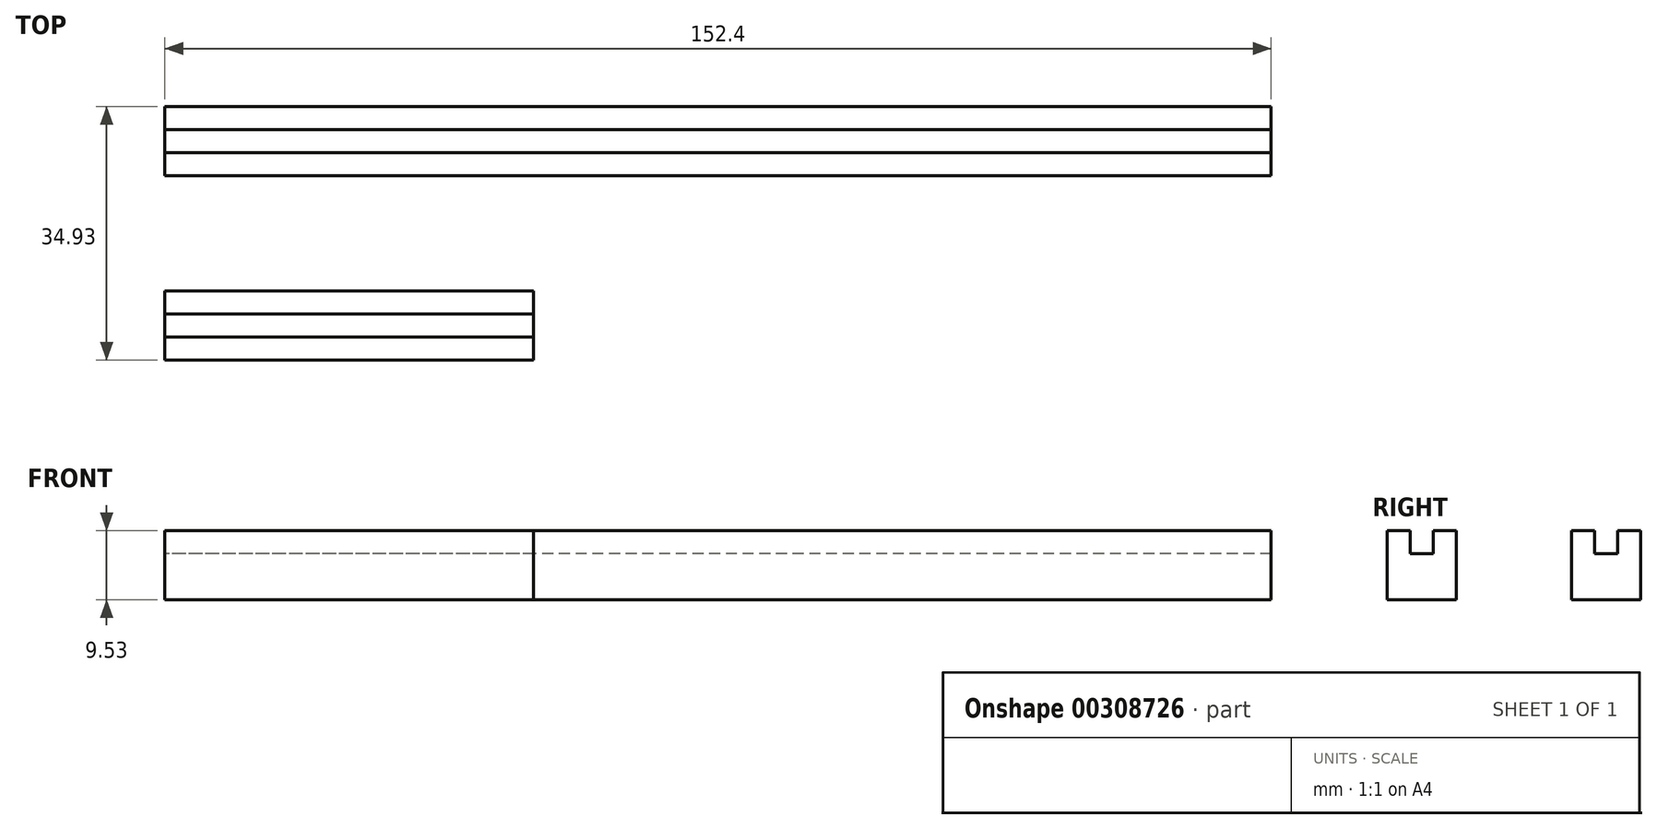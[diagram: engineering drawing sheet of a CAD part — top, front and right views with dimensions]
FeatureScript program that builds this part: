
annotation { "Feature Type Name" : "Feature", "Feature Type Description" : "" }
export const myFeature = defineFeature(function(context is Context, id is Id, definition is map)
    precondition{}
    {
        {
            var Q0;
            Q0=qCreatedBy(makeId("Right.planeOp"),FACE);
            var sketch = newSketch(context, id + "F0", { "sketchPlane" : qUnion([Q0])});
            skLineSegment(sketch, "E0", {"start": v(0, 0) * mm, "end": v(0, 9.53) * mm});
            skLineSegment(sketch, "E1", {"start": v(0, 9.53) * mm, "end": v(3.18, 9.53) * mm});
            skLineSegment(sketch, "E2", {"start": v(3.18, 9.53) * mm, "end": v(3.18, 6.35) * mm});
            skLineSegment(sketch, "E3", {"start": v(3.18, 6.35) * mm, "end": v(6.35, 6.35) * mm});
            skLineSegment(sketch, "E4", {"start": v(6.35, 6.35) * mm, "end": v(6.35, 9.53) * mm});
            skLineSegment(sketch, "E5", {"start": v(6.35, 9.53) * mm, "end": v(9.53, 9.53) * mm});
            skLineSegment(sketch, "E6", {"start": v(9.53, 9.53) * mm, "end": v(9.53, 0) * mm});
            skLineSegment(sketch, "E7", {"start": v(9.53, 0) * mm, "end": v(0, 0) * mm});
            skSolve(sketch);
        }
        {
            var Q0;
            Q0=makeQuery(id+"F0.imprint","IMPRINT",FACE,{"disambiguationData":[TD([[makeQuery(id+"F0.imprint","IMPRINT",EDGE,{"derivedFrom":sQuery(id+"F0.wireOp",EDGE,"E0")}),-1.0]])]});
            extrude(context, id + "F1", {"entities" : qUnion([Q0]), "depth" : 50.8 * mm});
        }
        {
            var Q0;
            Q0=makeQuery(id+"F1.opExtrude","SWEPT_BODY",BODY,{"disambiguationData":[OSD([sQuery(id+"F0.wireOp",EDGE,"E0"),sQuery(id+"F0.wireOp",EDGE,"E1"),sQuery(id+"F0.wireOp",EDGE,"E2"),sQuery(id+"F0.wireOp",EDGE,"E3"),sQuery(id+"F0.wireOp",EDGE,"E4"),sQuery(id+"F0.wireOp",EDGE,"E5"),sQuery(id+"F0.wireOp",EDGE,"E6"),sQuery(id+"F0.wireOp",EDGE,"E7")])]});
            transform(context, id + "F2", {"entities" : qUnion([Q0]), "transformType" : TransformType.COPY});
        }
        {
            var Q0;
            Q0=makeQuery(id+"F2.opPattern","COPY",BODY,{"derivedFrom":makeQuery(id+"F1.opExtrude","SWEPT_BODY",BODY,{"disambiguationData":[OSD([sQuery(id+"F0.wireOp",EDGE,"E0"),sQuery(id+"F0.wireOp",EDGE,"E1"),sQuery(id+"F0.wireOp",EDGE,"E2"),sQuery(id+"F0.wireOp",EDGE,"E3"),sQuery(id+"F0.wireOp",EDGE,"E4"),sQuery(id+"F0.wireOp",EDGE,"E5"),sQuery(id+"F0.wireOp",EDGE,"E6"),sQuery(id+"F0.wireOp",EDGE,"E7")])]}),"instanceName":"1"});
            var Q1;
            Q1=makeQuery(id+"F1.opExtrude","CAP_EDGE",EDGE,{"disambiguationData":[OSD([sQuery(id+"F0.wireOp",EDGE,"E7")])],"isStart":false});
            var Q2;
            Q2=makeQuery(id+"F1.opExtrude","CAP_EDGE",EDGE,{"disambiguationData":[OSD([sQuery(id+"F0.wireOp",EDGE,"E7")])],"isStart":false});
            transform(context, id + "F3", {"entities" : qUnion([Q0]), "transformType" : TransformType.TRANSLATION_DISTANCE, "transformDirection" : qUnion([Q2]), "distance" : 25.4 * mm, "makeCopy" : false});
        }
        {
            var Q0;
            Q0=makeQuery(id+"F1.opExtrude","CAP_FACE",FACE,{"disambiguationData":[OSD([sQuery(id+"F0.wireOp",EDGE,"E0"),sQuery(id+"F0.wireOp",EDGE,"E1"),sQuery(id+"F0.wireOp",EDGE,"E2"),sQuery(id+"F0.wireOp",EDGE,"E3"),sQuery(id+"F0.wireOp",EDGE,"E4"),sQuery(id+"F0.wireOp",EDGE,"E5"),sQuery(id+"F0.wireOp",EDGE,"E6"),sQuery(id+"F0.wireOp",EDGE,"E7")])],"isStart":false});
            var sketch = newSketch(context, id + "F4", { "sketchPlane" : qUnion([Q0])});
            skSolve(sketch);
        }
        {
            var Q0;
            Q0=makeQuery(id+"F4.imprint","IMPRINT",FACE,{"disambiguationData":[TD([[makeQuery(id+"F4.imprint","IMPRINT",EDGE,{"derivedFrom":makeQuery(id+"F1.opExtrude","CAP_EDGE",EDGE,{"disambiguationData":[OSD([sQuery(id+"F0.wireOp",EDGE,"E0")])],"isStart":false})}),-1.0]])]});
            extrude(context, id + "F5", {"entities" : qUnion([Q0]), "operationType" : NewBodyOperationType.ADD, "depth" : 101.6 * mm});
        }
    });
